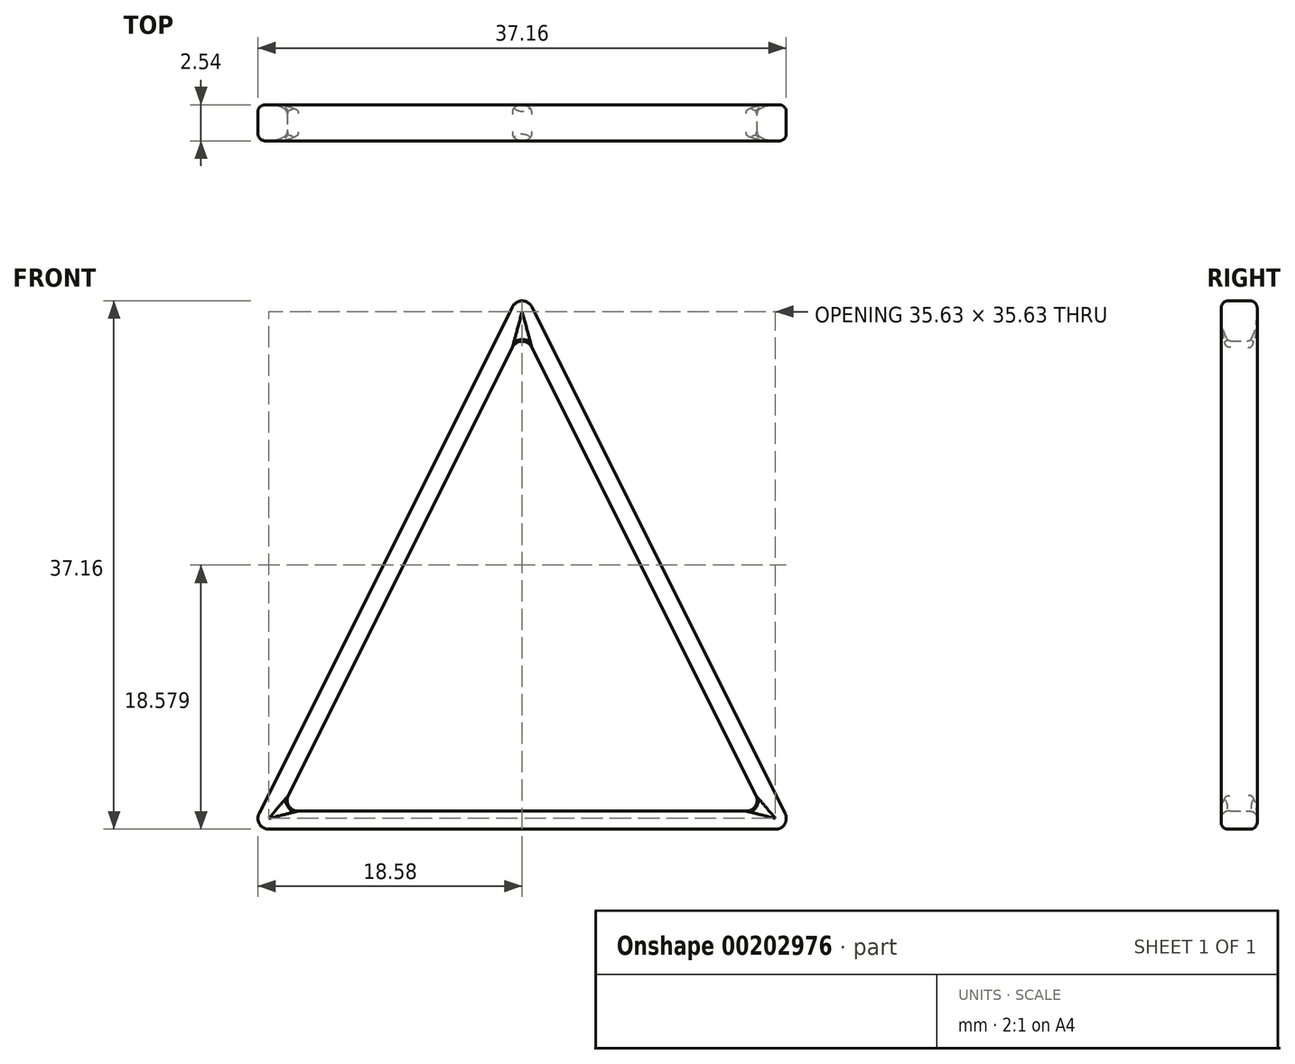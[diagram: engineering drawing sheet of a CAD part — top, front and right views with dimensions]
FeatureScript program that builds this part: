
annotation { "Feature Type Name" : "Feature", "Feature Type Description" : "" }
export const myFeature = defineFeature(function(context is Context, id is Id, definition is map)
    precondition{}
    {
        {
            var Q0;
            Q0=qCreatedBy(makeId("Front.planeOp"),FACE);
            var sketch = newSketch(context, id + "F0", { "sketchPlane" : qUnion([Q0])});
            skLineSegment(sketch, "E0", {"start": v(0, 0) * mm, "end": v(38.1, 0) * mm});
            skLineSegment(sketch, "E1", {"start": v(19.05, 38.1) * mm, "end": v(0, 0) * mm});
            skLineSegment(sketch, "E2", {"start": v(19.05, 38.1) * mm, "end": v(38.1, 0) * mm});
            skPoint(sketch, "E3.orphan", {"position": v(38.1, 38.1) * mm});
            skPoint(sketch, "E4.0.start.orphan", {"position": v(0, 38.1) * mm});
            skLineSegment(sketch, "E5.0", {"start": v(2.05, 1.27) * mm, "end": v(36.05, 1.27) * mm});
            skLineSegment(sketch, "E6.trimOffspring", {"start": v(19.05, 35.26) * mm, "end": v(36.05, 1.27) * mm});
            skLineSegment(sketch, "E7.trimOffspring", {"start": v(19.05, 35.26) * mm, "end": v(2.05, 1.27) * mm});
            skSolve(sketch);
        }
        {
            var Q0;
            Q0=makeQuery(id+"F0.imprint","IMPRINT",FACE,{"disambiguationData":[TD([[makeQuery(id+"F0.imprint","IMPRINT",EDGE,{"derivedFrom":sQuery(id+"F0.wireOp",EDGE,"E0")}),1.0]])]});
            extrude(context, id + "F1", {"entities" : qUnion([Q0]), "depth" : 2.54 * mm});
        }
        {
            var Q0;
            Q0=makeQuery(id+"F1.opExtrude","CAP_EDGE",EDGE,{"disambiguationData":[OSD([sQuery(id+"F0.wireOp",EDGE,"E1")])],"isStart":false});
            var Q1;
            Q1=makeQuery(id+"F1.opExtrude","CAP_EDGE",EDGE,{"disambiguationData":[OSD([sQuery(id+"F0.wireOp",EDGE,"E7.trimOffspring")])],"isStart":false});
            var Q2;
            Q2=makeQuery(id+"F1.opExtrude","CAP_EDGE",EDGE,{"disambiguationData":[OSD([sQuery(id+"F0.wireOp",EDGE,"E2")])],"isStart":false});
            var Q3;
            Q3=makeQuery(id+"F1.opExtrude","CAP_EDGE",EDGE,{"disambiguationData":[OSD([sQuery(id+"F0.wireOp",EDGE,"E6.trimOffspring")])],"isStart":false});
            var Q4;
            Q4=makeQuery(id+"F1.opExtrude","CAP_EDGE",EDGE,{"disambiguationData":[OSD([sQuery(id+"F0.wireOp",EDGE,"E0")])],"isStart":false});
            var Q5;
            Q5=makeQuery(id+"F1.opExtrude","CAP_EDGE",EDGE,{"disambiguationData":[OSD([sQuery(id+"F0.wireOp",EDGE,"E5.0")])],"isStart":false});
            fillet(context, id + "F2", {"entities" : qUnion([Q0, Q1, Q2, Q3, Q4, Q5]), "radius" : 0.5 * mm, "tangentPropagation" : true, "allowEdgeOverflow" : false});
        }
        {
            var Q0;
            Q0=makeQuery(id+"F1.opExtrude","CAP_FACE",FACE,{"disambiguationData":[OSD([sQuery(id+"F0.wireOp",EDGE,"E0"),sQuery(id+"F0.wireOp",EDGE,"E1"),sQuery(id+"F0.wireOp",EDGE,"E2"),sQuery(id+"F0.wireOp",EDGE,"E5.0"),sQuery(id+"F0.wireOp",EDGE,"E6.trimOffspring"),sQuery(id+"F0.wireOp",EDGE,"E7.trimOffspring")])],"isStart":true});
            fillet(context, id + "F3", {"entities" : qUnion([Q0]), "radius" : 0.5 * mm, "tangentPropagation" : true, "allowEdgeOverflow" : false});
        }
        {
            var Q0;
            Q0=makeQuery(id+"F1.opExtrude","SWEPT_EDGE",EDGE,{"disambiguationData":[OSD([sQuery(id+"F0.wireOp",EDGE,"E1"),sQuery(id+"F0.wireOp",EDGE,"E2")])]});
            var Q1;
            Q1=makeQuery(id+"F1.opExtrude","SWEPT_EDGE",EDGE,{"disambiguationData":[OSD([sQuery(id+"F0.wireOp",EDGE,"E6.trimOffspring"),sQuery(id+"F0.wireOp",EDGE,"E7.trimOffspring")])]});
            var Q2;
            Q2=makeQuery(id+"F1.opExtrude","SWEPT_EDGE",EDGE,{"disambiguationData":[OSD([sQuery(id+"F0.wireOp",EDGE,"E0"),sQuery(id+"F0.wireOp",EDGE,"E2")])]});
            var Q3;
            Q3=makeQuery(id+"F1.opExtrude","SWEPT_EDGE",EDGE,{"disambiguationData":[OSD([sQuery(id+"F0.wireOp",EDGE,"E0"),sQuery(id+"F0.wireOp",EDGE,"E1")])]});
            var Q4;
            Q4=makeQuery(id+"F1.opExtrude","SWEPT_EDGE",EDGE,{"disambiguationData":[OSD([sQuery(id+"F0.wireOp",EDGE,"E5.0"),sQuery(id+"F0.wireOp",EDGE,"E6.trimOffspring")])]});
            var Q5;
            Q5=makeQuery(id+"F1.opExtrude","SWEPT_EDGE",EDGE,{"disambiguationData":[OSD([sQuery(id+"F0.wireOp",EDGE,"E5.0"),sQuery(id+"F0.wireOp",EDGE,"E7.trimOffspring")])]});
            fillet(context, id + "F4", {"entities" : qUnion([Q0, Q1, Q2, Q3, Q4, Q5]), "radius" : 0.76 * mm, "tangentPropagation" : true, "allowEdgeOverflow" : false});
        }
    });
